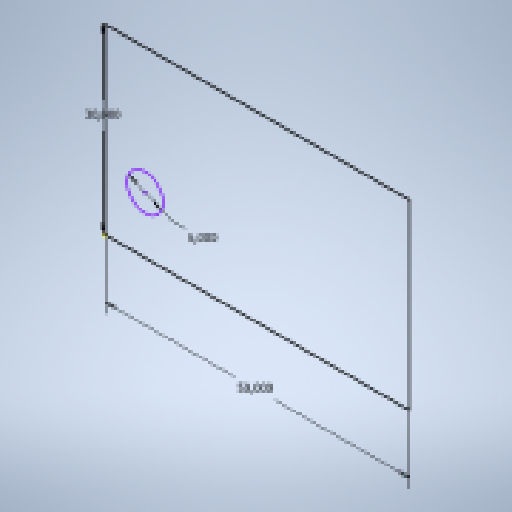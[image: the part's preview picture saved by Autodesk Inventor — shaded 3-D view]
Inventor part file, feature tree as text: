
AUTODESK INVENTOR PART (.ipt)
format: ipt  version: 2025.2 (Build 292293000, 293)  size: 216,064 bytes
history: native  units: in
note: dims shown in document units (in); Inventor stores cm internally (conversion verified against a paired STEP export)
features: sketch x4, extrude x3, other x2, projected_geometry x1, reference x1
ambient origin geometry x8: Origin, YZ Plane, XZ Plane, XY Plane, X Axis, Y Axis, Z Axis, Center Point
bodies: Solid1 (feature_tree)
feature tree (11):
  extrude  "Extrusion1"  Depth=50.0in
  extrude  "Extrusion2"  Depth=6.0in
  extrude  "Extrusion3"  Depth=5.0in
  sketch  "Sketch1"  dims[d0=30.0in d1=50.0in]
  sketch  "Sketch2"  dims[d15=1.1811in d17=180.0deg d19=5.0in]
  sketch  "Sketch Circular Pattern1"  dims[d7=5.0in d8=0.0in d14=6.0in]
  sketch  "Sketch4"  dims[d20=15.0in d21=4.0in d22=0.0in d23=8.0in d24=1.1in d25=8.0in d26=1.1in d27=8.0in d28=1.1in d29=10.0in d30=3.5in d31=7.0in d32=4.0in d33=10.0in d34=3.5in d35=7.0in d36=4.0in d37=4.0in d38=4.0in d39=1.0in d40=0.0in]
  projected_geometry  "Projected Loop2"
  reference  "Reference1"
  other  "Assembly2"
  other  "Zaślepki:1"
